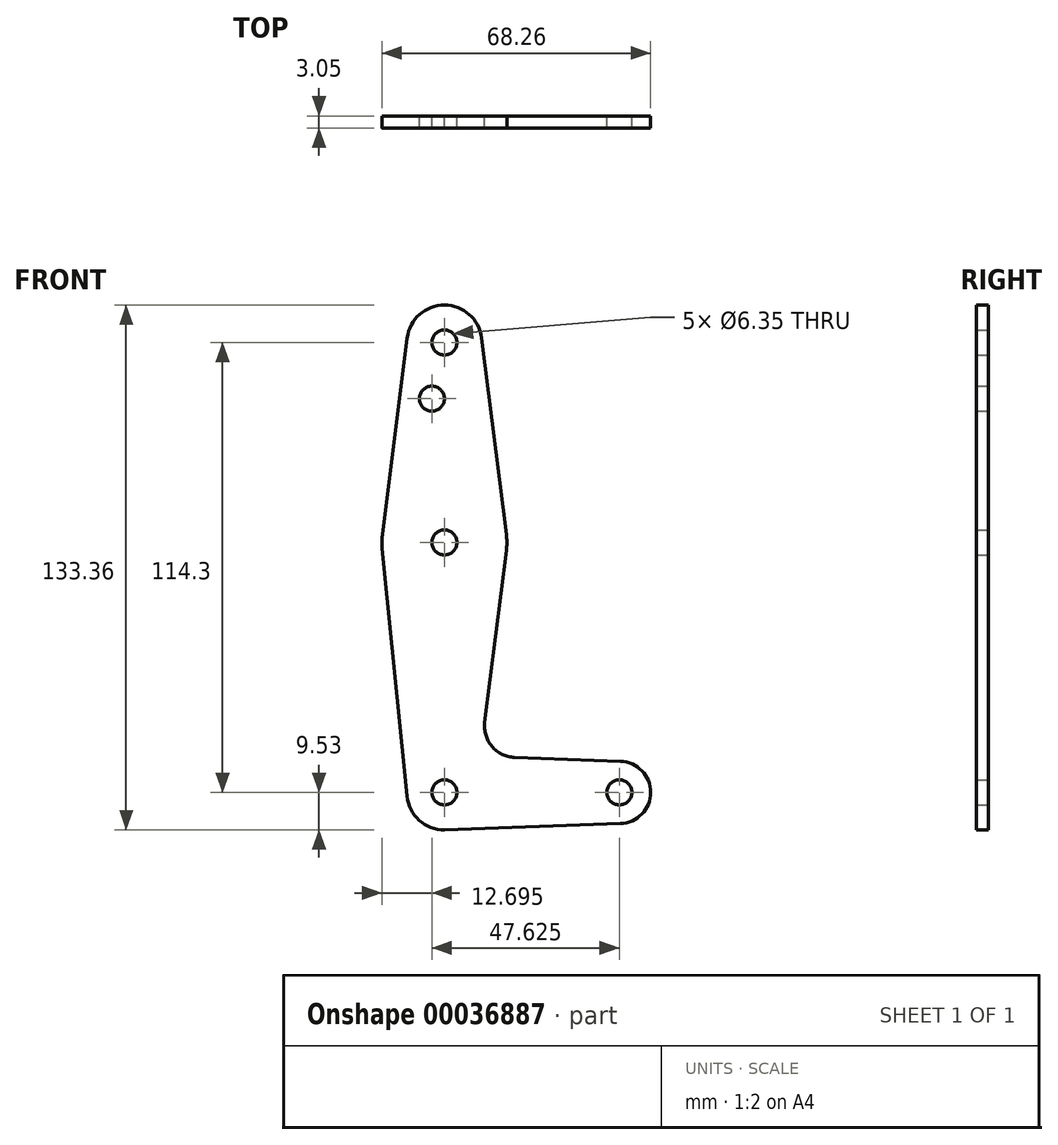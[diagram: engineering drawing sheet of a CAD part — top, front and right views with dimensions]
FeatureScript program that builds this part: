
annotation { "Feature Type Name" : "Feature", "Feature Type Description" : "" }
export const myFeature = defineFeature(function(context is Context, id is Id, definition is map)
    precondition{}
    {
        {
            var Q0;
            Q0=qCreatedBy(makeId("Front.planeOp"),FACE);
            var sketch = newSketch(context, id + "F0", { "sketchPlane" : qUnion([Q0])});
            skCircle(sketch, "E0", {"center": v(0, 0) * mm, "radius": 9.53 * mm});
            skCircle(sketch, "E1", {"center": v(0, 63.5) * mm, "radius": 15.88 * mm});
            skCircle(sketch, "E2", {"center": v(0, 114.3) * mm, "radius": 9.53 * mm});
            skCircle(sketch, "E3", {"center": v(44.45, 0) * mm, "radius": 7.94 * mm});
            skLineSegment(sketch, "E4", {"start": v(0, 114.3) * mm, "end": v(0, 0) * mm, "construction": true});
            skLineSegment(sketch, "E5", {"start": v(0, 0) * mm, "end": v(44.45, 0) * mm, "construction": true});
            skLineSegment(sketch, "E6", {"start": v(-9.45, 115.5) * mm, "end": v(-15.75, 65.48) * mm});
            skLineSegment(sketch, "E7", {"start": v(9.45, 115.5) * mm, "end": v(15.75, 65.48) * mm});
            skLineSegment(sketch, "E8", {"start": v(10.25, 17.83) * mm, "end": v(15.75, 61.52) * mm});
            skLineSegment(sketch, "E9", {"start": v(-9.48, -0.95) * mm, "end": v(-15.8, 61.91) * mm});
            skLineSegment(sketch, "E10", {"start": v(17.85, 8.89) * mm, "end": v(44.73, 7.93) * mm});
            skLineSegment(sketch, "E11", {"start": v(0, -9.53) * mm, "end": v(44.73, -7.93) * mm});
            skCircle(sketch, "E12", {"center": v(0, 114.3) * mm, "radius": 3.18 * mm});
            skCircle(sketch, "E13", {"center": v(-3.17, 100.03) * mm, "radius": 3.18 * mm});
            skCircle(sketch, "E14", {"center": v(0, 63.5) * mm, "radius": 3.18 * mm});
            skCircle(sketch, "E15", {"center": v(44.45, 0) * mm, "radius": 3.18 * mm});
            skCircle(sketch, "E16", {"center": v(0, 0) * mm, "radius": 3.18 * mm});
            skPoint(sketch, "E17.newPointB", {"position": v(7.88, -0.95) * mm});
            skArc(sketch, "E17.filletArc", {"start": v(10.25, 17.83) * mm, "mid": v(12.08, 11.68) * mm, "end": v(17.85, 8.89) * mm});
            skSolve(sketch);
        }
        {
            var Q0;
            {var subQ0=sQuery(id+"F0.wireOp",EDGE,"E6");Q0=makeQuery(id+"F0.imprint","IMPRINT",FACE,{"disambiguationData":[TD([[makeQuery(id+"F0.imprint","IMPRINT",EDGE,{"derivedFrom":subQ0}),1.0]])]});}
            var Q1;
            Q1=makeQuery(id+"F0.imprint","IMPRINT",FACE,{"disambiguationData":[TD([[makeQuery(id+"F0.imprint","IMPRINT",EDGE,{"derivedFrom":sQuery(id+"F0.wireOp",EDGE,"E12")}),-1.0]])]});
            var Q2;
            Q2=makeQuery(id+"F0.imprint","IMPRINT",FACE,{"disambiguationData":[TD([[makeQuery(id+"F0.imprint","IMPRINT",EDGE,{"derivedFrom":sQuery(id+"F0.wireOp",EDGE,"E14")}),-1.0]])]});
            var Q3;
            {var subQ7=sQuery(id+"F0.wireOp",EDGE,"E8");Q3=makeQuery(id+"F0.imprint","IMPRINT",FACE,{"disambiguationData":[TD([[makeQuery(id+"F0.imprint","IMPRINT",EDGE,{"derivedFrom":subQ7}),1.0]])]});}
            var Q4;
            Q4=makeQuery(id+"F0.imprint","IMPRINT",FACE,{"disambiguationData":[TD([[makeQuery(id+"F0.imprint","IMPRINT",EDGE,{"derivedFrom":sQuery(id+"F0.wireOp",EDGE,"E15")}),-1.0]])]});
            var Q5;
            Q5=makeQuery(id+"F0.imprint","IMPRINT",FACE,{"disambiguationData":[TD([[makeQuery(id+"F0.imprint","IMPRINT",EDGE,{"derivedFrom":sQuery(id+"F0.wireOp",EDGE,"E16")}),-1.0]])]});
            extrude(context, id + "F1", {"entities" : qUnion([Q0, Q1, Q2, Q3, Q4, Q5]), "depth" : 3.05 * mm});
        }
    });
